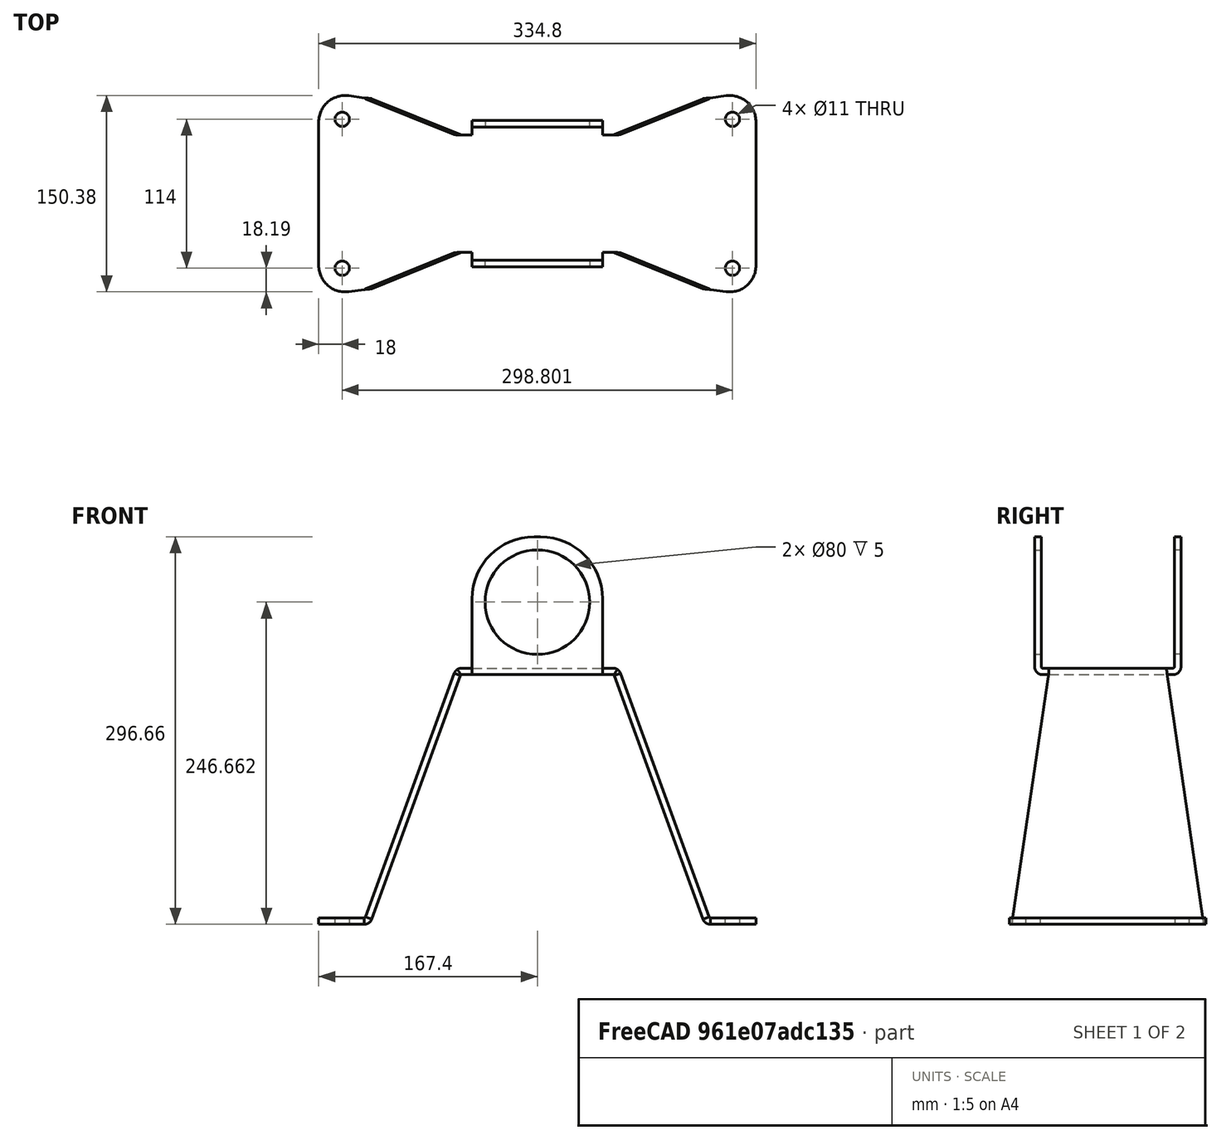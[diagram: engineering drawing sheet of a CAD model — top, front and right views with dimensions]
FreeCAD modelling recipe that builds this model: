
FCSTD DOCUMENT  (FreeCAD 0.19R22960 (Git))
Label: tv-halter
License: All rights reserved
LicenseURL: http://en.wikipedia.org/wiki/All_rights_reserved
objects: TechDraw::DrawViewDimension×14, Sketcher::SketchObject×7, PartDesign::FeaturePython×6, TechDraw::DrawProjGroupItem×5, TechDraw::DrawProjGroup×5, PartDesign::Plane×2, PartDesign::Pad×1, PartDesign::Mirrored×1, PartDesign::Body×1, TechDraw::DrawSVGTemplate×1, TechDraw::DrawPage×1
note: 19 computed .brp shape members not serialized (recipe doc carries the construction recipe); baked Part::Feature solids carry a one-line shape summary decoded from their .brp

FEATURE [Sketcher::SketchObject] Sketch  label="SketchModel"
  MapMode = 5
  Support = -> [XY_Plane]
  sketch-geometry (17):
    g0: LineSegment StartX=-277.045 StartY=75 StartZ=0 EndX=-60 EndY=45 EndZ=0
    g1: LineSegment StartX=-60 StartY=45 StartZ=0 EndX=-50 EndY=45 EndZ=0
    g2: LineSegment StartX=-50 StartY=45 StartZ=0 EndX=-50 EndY=107.5 EndZ=0
    g3: LineSegment StartX=-2.5 StartY=155 StartZ=0 EndX=2.5 EndY=155 EndZ=0
    g4: LineSegment StartX=50 StartY=107.5 StartZ=0 EndX=50 EndY=45 EndZ=0
    g5: LineSegment StartX=50 StartY=45 StartZ=0 EndX=60 EndY=45 EndZ=0
    g6: LineSegment StartX=60 StartY=45 StartZ=0 EndX=277.045 EndY=75 EndZ=0
    g7: LineSegment StartX=300 StartY=55 StartZ=0 EndX=300 EndY=0 EndZ=0
    g8: LineSegment StartX=300 StartY=0 StartZ=0 EndX=-300 EndY=0 EndZ=0
    g9: LineSegment StartX=-300 StartY=0 StartZ=0 EndX=-300 EndY=55 EndZ=0
    g10: ArcOfCircle CenterX=-2.5 CenterY=107.5 CenterZ=0 NormalX=0 NormalY=0 NormalZ=1 AngleXU=0 Radius=47.5 StartAngle=1.5708 EndAngle=3.14159
    g11: ArcOfCircle CenterX=2.5 CenterY=107.5 CenterZ=0 NormalX=0 NormalY=0 NormalZ=1 AngleXU=0 Radius=47.5 StartAngle=0 EndAngle=1.5708
    g12: ArcOfCircle CenterX=-279.81 CenterY=55 CenterZ=0 NormalX=0 NormalY=0 NormalZ=1 AngleXU=0 Radius=20.1901 StartAngle=1.43345 EndAngle=3.14159
    g13: ArcOfCircle CenterX=279.81 CenterY=55 CenterZ=0 NormalX=0 NormalY=0 NormalZ=1 AngleXU=0 Radius=20.1901 StartAngle=0 EndAngle=1.70815
    g14: Circle CenterX=1.5e-15 CenterY=105 CenterZ=0 NormalX=0 NormalY=0 NormalZ=1 AngleXU=0 Radius=40
    g15: Circle CenterX=282 CenterY=57 CenterZ=0 NormalX=0 NormalY=0 NormalZ=1 AngleXU=0 Radius=5.5
    g16: Circle CenterX=-282 CenterY=57 CenterZ=0 NormalX=0 NormalY=0 NormalZ=1 AngleXU=0 Radius=5.5
  constraints (50):
    c: Coincident(g0,g1)
    c: Horizontal(g1)
    c: Coincident(g1,g2)
    c: Vertical(g2)
    c: Horizontal(g3)
    c: Coincident(g4,g5)
    c: Coincident(g5,g6)
    c: Vertical(g7)
    c: Coincident(g7,g8)
    c: Horizontal(g8)
    c: Coincident(g8,g9)
    c: Vertical(g4)
    c: Equal(g2,g4)
    c: DistanceX(g8,g8) = 600
    c: Vertical(g9)
    c: Equal(g7,g9)
    c: DistanceY(g8,g0) = 45
    c: DistanceX(g1,g1) = 10
    c: Equal(g1,g5)
    c: Horizontal(g5)
    c: DistanceX(g8,g1) = 250
    c: DistanceX(g8,g-1) = 300
    c: DistanceY(g-1,g7) = 0
    c: Tangent(g3,g10) = 1.5708
    c: Tangent(g2,g10) = 1.5708
    c: Tangent(g3,g11) = 1.5708
    c: Tangent(g4,g11) = 1.5708
    c: Equal(g2,g4)
    c: DistanceX(g1,g4) = 100
    c: DistanceY(g-1,g4) = 45
    c: Tangent(g0,g12) = 1.5708
    c: Tangent(g9,g12) = 1.5708
    c: Tangent(g6,g13) = 1.5708
    c: Tangent(g7,g13) = 1.5708
    c: Equal(g12,g13)
    c: Equal(g9,g7)
    c: DistanceY(g7,g7) = 55
    c: DistanceY(g7,g6) = 75
    c: Equal(g0,g6)
    c: DistanceX(g3,g3) = 5
    c: DistanceY(g-1,g3) = 155
    c: Diameter(g14) = 80
    c: DistanceX(g14,g4) = 50
    c: DistanceY(g-1,g14) = 105
    c: Diameter(g15) = 11
    c: DistanceY(g15,g6) = 18
    c: Equal(g15,g16)
    c: DistanceX(g15,g7) = 18
    c: DistanceY(g16,g0) = 18
    c: DistanceX(g9,g16) = 18
FEATURE [PartDesign::Pad] Pad
  Direction = (1,1,1)
  Length = 5
  Length2 = 100
  Profile = -> Sketch
  Reversed = true
  Type = 0
FEATURE [PartDesign::Mirrored] Mirrored
  BaseFeature = -> Pad
  MirrorPlane = -> XZ_Plane
  Originals = -> [Pad]
  Refine = true
FEATURE [Sketcher::SketchObject] Sketch001  label="SketchBiegungOben"
  ExternalGeometry = -> [Mirrored]
  MapMode = 5
  Support = -> [XY_Plane]
  sketch-geometry (1):
    g0: LineSegment StartX=-55.7755 StartY=50 StartZ=0 EndX=60.8267 EndY=50 EndZ=0
  constraints (2):
    c: Horizontal(g0)
    c: DistanceY(g-3,g0) = 5
FEATURE [PartDesign::FeaturePython] Fold  # WARN: FeaturePython — macro-defined, semantics opaque (R4)
  BaseFeature = -> Mirrored
  BendLine = -> Sketch001
  Position = 0
  angle = 90
  baseObject = -> Mirrored [Face12]
  invert = false
  invertbend = false
  kfactor = 0.5
  radius = 1
  unfold = false
FEATURE [Sketcher::SketchObject] Sketch002  label="SketchBiegungUnten"
  ExternalGeometry = -> [Fold]
  MapMode = 5
  Support = -> [XY_Plane]
  sketch-geometry (1):
    g0: LineSegment StartX=-55.1933 StartY=-50 StartZ=0 EndX=57.3622 EndY=-50 EndZ=0
  constraints (2):
    c: Horizontal(g0)
    c: DistanceY(g0,g-3) = 5
FEATURE [PartDesign::FeaturePython] Fold001  # WARN: FeaturePython — macro-defined, semantics opaque (R4)
  BaseFeature = -> Fold
  BendLine = -> Sketch002
  Position = 0
  angle = 90
  baseObject = -> Fold [Face2]
  invert = false
  invertbend = false
  kfactor = 0.5
  radius = 1
  unfold = false
FEATURE [Sketcher::SketchObject] Sketch003  label="SketchBiegung1Links"
  ExternalGeometry = -> [Fold001]
  MapMode = 5
  Support = -> [XY_Plane]
  sketch-geometry (1):
    g0: LineSegment StartX=-58 StartY=46.2726 StartZ=0 EndX=-58 EndY=-48.525 EndZ=0
  constraints (2):
    c: Vertical(g0)
    c: DistanceX(g0,g-3) = 8
FEATURE [PartDesign::FeaturePython] Fold002  # WARN: FeaturePython — macro-defined, semantics opaque (R4)
  BaseFeature = -> Fold001
  BendLine = -> Sketch003
  Position = 0
  angle = 70
  baseObject = -> Fold001 [Face5]
  invert = true
  invertbend = false
  kfactor = 0.5
  radius = 1
  unfold = false
FEATURE [Sketcher::SketchObject] Sketch004  label="SketchBiegung1Rechts"
  ExternalGeometry = -> [Fold001]
  MapMode = 5
  Support = -> [XY_Plane]
  sketch-geometry (1):
    g0: LineSegment StartX=58 StartY=-51.7839 StartZ=0 EndX=58 EndY=60.7718 EndZ=0
  constraints (2):
    c: Vertical(g0)
    c: DistanceX(g-3,g0) = 8
FEATURE [PartDesign::FeaturePython] Fold003  # WARN: FeaturePython — macro-defined, semantics opaque (R4)
  BaseFeature = -> Fold002
  BendLine = -> Sketch004
  Position = 0
  angle = 70
  baseObject = -> Fold002 [Face5]
  invert = true
  invertbend = false
  kfactor = 0.5
  radius = 1
  unfold = false
FEATURE [PartDesign::Plane] DatumPlane  label="DatumPlaneLinks"
  Length = 296.814
  MapMode = 5
  Placement = pos=(-54.9251,-1.29e-14,19.9911) rot=(0.497543,-0.497543,-0.710565;1.90603rad)
  ResizeMode = 0
  Support = -> [Fold003]
  Width = 550.72
FEATURE [Sketcher::SketchObject] Sketch005  label="SketchBiegung2Links"
  MapMode = 5
  Placement = pos=(-54.9251,-1.29e-14,19.9911) rot=(0.497543,-0.497543,-0.710565;1.90603rad)
  Support = -> [DatumPlane]
  sketch-geometry (1):
    g0: LineSegment StartX=-78.6082 StartY=-224 StartZ=0 EndX=77.3284 EndY=-224 EndZ=0
  constraints (2):
    c: Horizontal(g0)
    c: DistanceY(g0,g-1) = 224
FEATURE [PartDesign::FeaturePython] Fold004  # WARN: FeaturePython — macro-defined, semantics opaque (R4)
  BaseFeature = -> Fold003
  BendLine = -> Sketch005
  Position = 0
  angle = 70
  baseObject = -> Fold003 [Face36]
  invert = false
  invertbend = false
  kfactor = 0.5
  radius = 1
  unfold = false
FEATURE [PartDesign::Plane] DatumPlane001  label="DatumPlaneRechts"
  Length = 296.814
  MapMode = 5
  Placement = pos=(54.9251,-1.29e-14,19.9911) rot=(0.497543,0.497543,0.710565;1.90603rad)
  ResizeMode = 0
  Support = -> [Fold004]
  Width = 550.72
FEATURE [Sketcher::SketchObject] Sketch006  label="SketchBiegung2Rechts"
  MapMode = 5
  Placement = pos=(54.9251,-1.29e-14,19.9911) rot=(0.497543,0.497543,0.710565;1.90603rad)
  Support = -> [DatumPlane001]
  sketch-geometry (1):
    g0: LineSegment StartX=-82.2591 StartY=-224 StartZ=0 EndX=83.665 EndY=-224 EndZ=0
  constraints (2):
    c: Horizontal(g0)
    c: DistanceY(g0,g-1) = 224
FEATURE [PartDesign::FeaturePython] Fold005  # WARN: FeaturePython — macro-defined, semantics opaque (R4)
  BaseFeature = -> Fold004
  BendLine = -> Sketch006
  Position = 0
  angle = 70
  baseObject = -> Fold004 [Face43]
  invert = false
  invertbend = false
  kfactor = 0.5
  radius = 1
  unfold = false
FEATURE [PartDesign::Body] Body
  Group = -> [Sketch,Pad,Mirrored,Sketch001,Fold,Sketch002,Fold001,Sketch003,Fold002,Sketch004,Fold003,DatumPlane,Sketch005,Fold004,DatumPlane001,Sketch006,Fold005]
  Origin = -> Origin
  Tip = -> Fold005
FEATURE [TechDraw::DrawSVGTemplate] Template
  EditableTexts = AUTHOR_NAME=dataliquid GmbH; DN=000; DRAWING_TITLE=TV Wandhalter; FC-DATE=24/01/2023; FC-REV=REV 1.0; FC-SC=SCALE; FC-SH=X / Y; FC-SI=A2; FreeCAD_DRAWING=TV Wandhalterung Stangenfuehrung; PN=000; SI-4=Angaben in mm
  Height = 420
  Orientation = 1
  Width = 594
FEATURE [TechDraw::DrawProjGroupItem] ProjItem  label="Layout"
  Caption = Layout
  CoarseView = false
  Direction = (0.577,-0.577,0.577)
  Focus = 100
  HardHidden = false
  IsoCount = 0
  IsoHidden = false
  IsoVisible = false
  LockPosition = true
  Perspective = false
  Rotation = 0
  RotationVector = (0.707,0.707,0)
  Scale = 0.5
  ScaleType = 2
  SeamHidden = false
  SeamVisible = true
  SmoothHidden = false
  SmoothVisible = true
  Source = -> [Mirrored]
  Type = 0
  X = 0
  XDirection = (0.707,0.707,0)
  Y = 0
FEATURE [TechDraw::DrawProjGroup] ProjGroup
  Anchor = -> ProjItem
  AutoDistribute = true
  LockPosition = false
  ProjectionType = 0
  Rotation = 0
  Scale = 0.5
  ScaleType = 0
  Source = -> [Mirrored]
  Views = -> [ProjItem]
  X = 446.129
  Y = 305.914
  spacingX = 15
  spacingY = 15
FEATURE [TechDraw::DrawProjGroupItem] ProjItem002  label="Objekt"
  Caption = Seitenansicht
  CoarseView = false
  Direction = (0.577,-0.577,0.577)
  Focus = 100
  HardHidden = false
  IsoCount = 0
  IsoHidden = false
  IsoVisible = false
  LockPosition = true
  Perspective = false
  Rotation = 0
  RotationVector = (0.707,0.707,0)
  Scale = 0.5
  ScaleType = 2
  SeamHidden = false
  SeamVisible = true
  SmoothHidden = false
  SmoothVisible = true
  Source = -> [Fold005]
  Type = 0
  X = 0
  XDirection = (0.707,0.707,0)
  Y = 0
FEATURE [TechDraw::DrawProjGroup] ProjGroup002
  Anchor = -> ProjItem002
  AutoDistribute = true
  LockPosition = false
  ProjectionType = 0
  Rotation = 0
  Scale = 0.5
  ScaleType = 0
  Source = -> [Fold005]
  Views = -> [ProjItem002]
  X = 234.78
  Y = 299.706
  spacingX = 15
  spacingY = 15
FEATURE [TechDraw::DrawProjGroupItem] ProjItem003  label="Oben"
  Caption = Oben
  CoarseView = false
  Direction = (0,1,0)
  Focus = 100
  HardHidden = false
  IsoCount = 0
  IsoHidden = false
  IsoVisible = false
  LockPosition = true
  Perspective = false
  Rotation = 0
  RotationVector = (1,0,0)
  Scale = 0.5
  ScaleType = 2
  SeamHidden = false
  SeamVisible = true
  SmoothHidden = false
  SmoothVisible = true
  Source = -> [Fold005]
  Type = 0
  X = 0
  XDirection = (-1,0,2e-16)
  Y = 0
FEATURE [TechDraw::DrawProjGroup] ProjGroup003
  Anchor = -> ProjItem003
  AutoDistribute = true
  LockPosition = false
  ProjectionType = 0
  Rotation = 0
  Scale = 0.5
  ScaleType = 0
  Source = -> [Fold005]
  Views = -> [ProjItem003]
  X = 133.613
  Y = 106.676
  spacingX = 15
  spacingY = 15
FEATURE [TechDraw::DrawViewDimension] Dimension007
  Arbitrary = false
  FormatSpec = %.2f
  Inverted = false
  LockPosition = false
  MeasureType = 1
  OverTolerance = 0
  References2D = -> [ProjItem003]
  Rotation = 0
  ScaleType = 0
  TheoreticalExact = false
  Type = 6
  UnderTolerance = 0
  X = -20.9201
  Y = 5.5363
FEATURE [TechDraw::DrawProjGroupItem] ProjItem004  label="Seitenansicht"
  Caption = Seitenansicht
  CoarseView = false
  Direction = (-1,0,1e-16)
  Focus = 100
  HardHidden = false
  IsoCount = 0
  IsoHidden = false
  IsoVisible = false
  LockPosition = true
  Perspective = false
  Rotation = 0
  RotationVector = (1,0,0)
  Scale = 0.6
  ScaleType = 2
  SeamHidden = false
  SeamVisible = true
  SmoothHidden = false
  SmoothVisible = true
  Source = -> [Fold005]
  Type = 0
  X = 0
  XDirection = (0,-1,1e-16)
  Y = 0
FEATURE [TechDraw::DrawProjGroup] ProjGroup004
  Anchor = -> ProjItem004
  AutoDistribute = true
  LockPosition = false
  ProjectionType = 0
  Rotation = 0
  Scale = 0.6
  ScaleType = 0
  Source = -> [Fold005]
  Views = -> [ProjItem004]
  X = 86.592
  Y = 300.291
  spacingX = 15
  spacingY = 15
FEATURE [TechDraw::DrawViewDimension] Dimension010
  Arbitrary = false
  FormatSpec = %.2f
  Inverted = false
  LockPosition = false
  MeasureType = 1
  OverTolerance = 0
  References2D = -> [ProjItem003]
  Rotation = 0
  ScaleType = 0
  TheoreticalExact = false
  Type = 6
  UnderTolerance = 0
  X = -75.3353
  Y = -57.2339
FEATURE [TechDraw::DrawViewDimension] Dimension011
  Arbitrary = false
  FormatSpec = ⌀%.2f
  Inverted = false
  LockPosition = false
  MeasureType = 1
  OverTolerance = 0
  References2D = -> [ProjItem003]
  Rotation = 0
  ScaleType = 0
  TheoreticalExact = false
  Type = 5
  UnderTolerance = 0
  X = 48.6488
  Y = 50.5566
FEATURE [TechDraw::DrawProjGroupItem] ProjItem005  label="Basis Layout (einfach)"
  Caption = Basis Layout (einfach)
  CoarseView = false
  Direction = (0,0,1)
  Focus = 100
  HardHidden = false
  IsoCount = 0
  IsoHidden = false
  IsoVisible = false
  LockPosition = true
  Perspective = false
  Rotation = 0
  RotationVector = (1,0,0)
  Scale = 0.5
  ScaleType = 2
  SeamHidden = false
  SeamVisible = true
  SmoothHidden = false
  SmoothVisible = true
  Source = -> [Sketch]
  Type = 0
  X = 0
  XDirection = (1,0,0)
  Y = 0
FEATURE [TechDraw::DrawProjGroup] ProjGroup005
  Anchor = -> ProjItem005
  AutoDistribute = true
  LockPosition = false
  ProjectionType = 0
  Rotation = 0
  Scale = 0.5
  ScaleType = 0
  Source = -> [Sketch]
  Views = -> [ProjItem005]
  X = 411.647
  Y = 142.736
  spacingX = 15
  spacingY = 15
FEATURE [TechDraw::DrawViewDimension] Dimension012
  Arbitrary = false
  FormatSpec = %.2f
  Inverted = false
  LockPosition = false
  MeasureType = 1
  OverTolerance = 0
  References2D = -> [ProjItem004]
  Rotation = 0
  ScaleType = 0
  TheoreticalExact = false
  Type = 6
  UnderTolerance = 0
  X = -14.823
  Y = 48.151
FEATURE [TechDraw::DrawViewDimension] Dimension013
  Arbitrary = false
  FormatSpec = %.2f
  Inverted = false
  LockPosition = false
  MeasureType = 1
  OverTolerance = 0
  References2D = -> [ProjItem004]
  Rotation = 0
  ScaleType = 0
  TheoreticalExact = false
  Type = 6
  UnderTolerance = 0
  X = 12.4861
  Y = 53.4175
FEATURE [TechDraw::DrawViewDimension] Dimension014
  Arbitrary = false
  FormatSpec = ⌀%.2f
  Inverted = false
  LockPosition = false
  MeasureType = 1
  OverTolerance = 0
  References2D = -> [ProjItem005]
  Rotation = 0
  ScaleType = 0
  TheoreticalExact = false
  Type = 5
  UnderTolerance = 0
  X = 123.053
  Y = 16.0255
FEATURE [TechDraw::DrawViewDimension] Dimension015
  Arbitrary = false
  FormatSpec = ⌀%.2f
  Inverted = false
  LockPosition = false
  MeasureType = 1
  OverTolerance = 0
  References2D = -> [ProjItem005]
  Rotation = 0
  ScaleType = 0
  TheoreticalExact = false
  Type = 5
  UnderTolerance = 0
  X = 42.9254
  Y = 34.3403
FEATURE [TechDraw::DrawViewDimension] Dimension016
  Arbitrary = false
  FormatSpec = %.2f
  Inverted = false
  LockPosition = false
  MeasureType = 1
  OverTolerance = 0
  References2D = -> [ProjItem005]
  Rotation = 0
  ScaleType = 0
  TheoreticalExact = false
  Type = 1
  UnderTolerance = 0
  X = 1.8e-15
  Y = -16.25
FEATURE [TechDraw::DrawViewDimension] Dimension017
  Arbitrary = false
  FormatSpec = %.2f
  Inverted = false
  LockPosition = false
  MeasureType = 1
  OverTolerance = 0
  References2D = -> [ProjItem005]
  Rotation = 0
  ScaleType = 0
  TheoreticalExact = false
  Type = 2
  UnderTolerance = 0
  X = -167.772
  Y = -3.43403
FEATURE [TechDraw::DrawViewDimension] Dimension018
  Arbitrary = false
  FormatSpec = %.2f
  Inverted = false
  LockPosition = false
  MeasureType = 1
  OverTolerance = 0
  References2D = -> [ProjItem005]
  Rotation = 0
  ScaleType = 0
  TheoreticalExact = false
  Type = 2
  UnderTolerance = 0
  X = -112.783
  Y = 13.1956
FEATURE [TechDraw::DrawViewDimension] Dimension019
  Arbitrary = false
  FormatSpec = %.2f
  Inverted = false
  LockPosition = false
  MeasureType = 1
  OverTolerance = 0
  References2D = -> [ProjItem005]
  Rotation = 0
  ScaleType = 0
  TheoreticalExact = false
  Type = 2
  UnderTolerance = 0
  X = -133.975
  Y = 13.919
FEATURE [TechDraw::DrawViewDimension] Dimension020
  Arbitrary = false
  FormatSpec = %.2f
  Inverted = false
  LockPosition = false
  MeasureType = 1
  OverTolerance = 0
  References2D = -> [ProjItem005]
  Rotation = 0
  ScaleType = 0
  TheoreticalExact = false
  Type = 1
  UnderTolerance = 0
  X = -3.43403
  Y = -51.9138
FEATURE [TechDraw::DrawViewDimension] Dimension
  Arbitrary = false
  FormatSpec = %.2f
  Inverted = false
  LockPosition = false
  MeasureType = 1
  OverTolerance = 0
  References2D = -> [ProjItem003]
  Rotation = 0
  ScaleType = 0
  TheoreticalExact = false
  Type = 6
  UnderTolerance = 0
  X = 25.8177
  Y = 5.29943
FEATURE [TechDraw::DrawViewDimension] Dimension021
  Arbitrary = false
  FormatSpec = %.2f
  Inverted = false
  LockPosition = false
  MeasureType = 1
  OverTolerance = 0
  References2D = -> [ProjItem003]
  Rotation = 0
  ScaleType = 0
  TheoreticalExact = false
  Type = 6
  UnderTolerance = 0
  X = 70.8628
  Y = -47.0325
FEATURE [TechDraw::DrawPage] Page
  KeepUpdated = true
  NextBalloonIndex = 1
  ProjectionType = 0
  Template = -> Template
  Views = -> [ProjGroup,ProjGroup002,ProjGroup003,Dimension007,ProjGroup004,Dimension010,Dimension011,ProjGroup005,Dimension012,Dimension013,Dimension014,Dimension015,Dimension016,Dimension017,Dimension018,Dimension019,Dimension020,Dimension,Dimension021]
